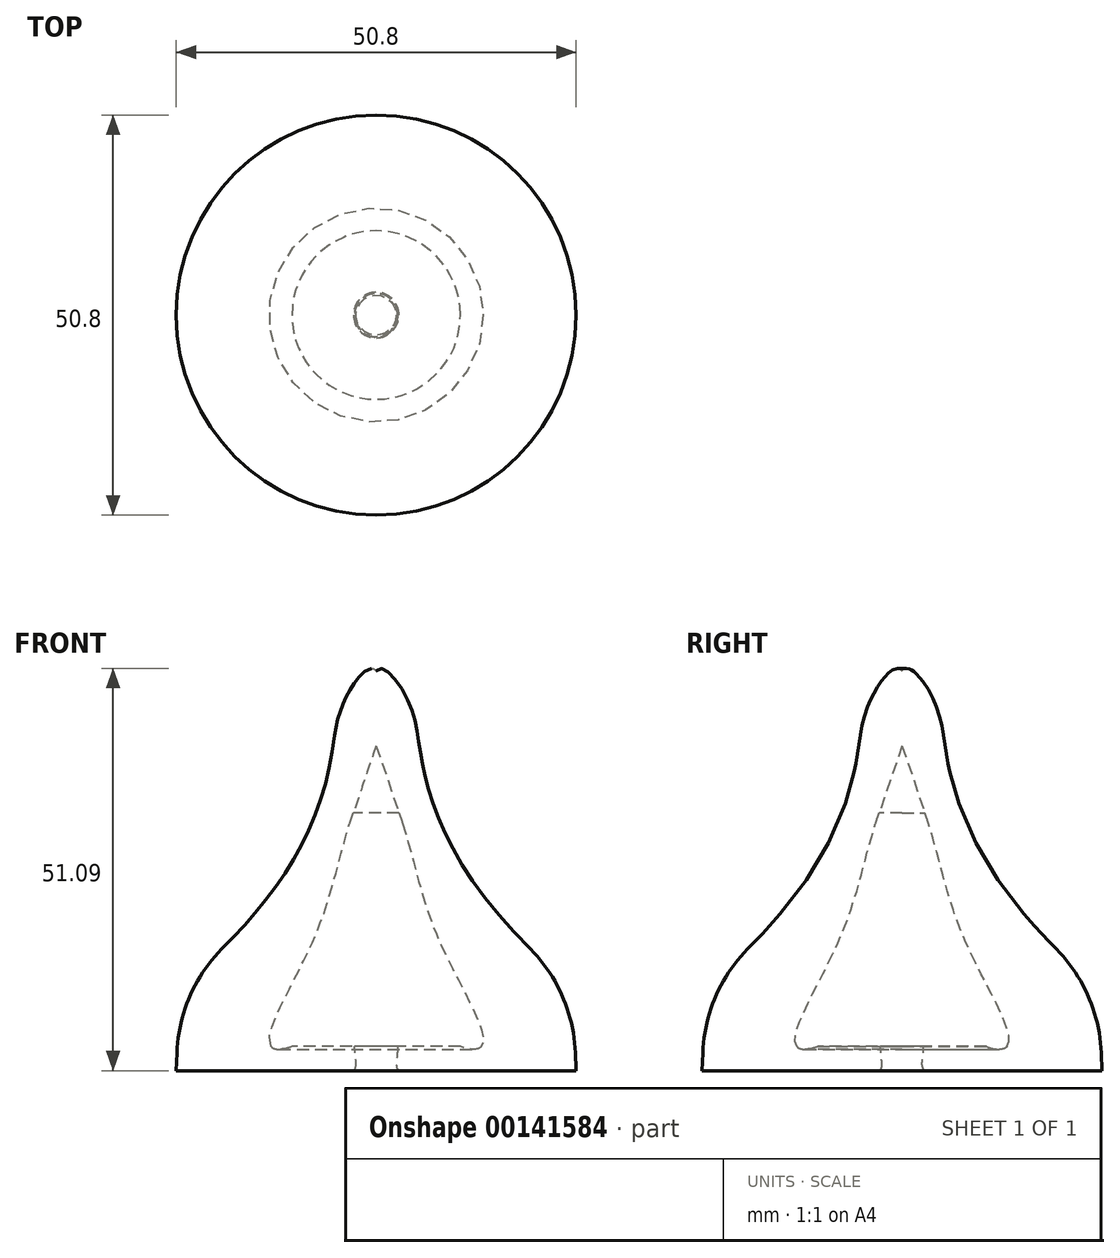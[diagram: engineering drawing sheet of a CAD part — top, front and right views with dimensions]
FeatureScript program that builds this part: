
annotation { "Feature Type Name" : "Feature", "Feature Type Description" : "" }
export const myFeature = defineFeature(function(context is Context, id is Id, definition is map)
    precondition{}
    {
        {
            var Q0;
            Q0=qCreatedBy(makeId("Front.planeOp"),FACE);
            var sketch = newSketch(context, id + "F0", { "sketchPlane" : qUnion([Q0])});
            skLineSegment(sketch, "E0", {"start": v(0, 50.8) * mm, "end": v(0, 41.27) * mm});
            skLineSegment(sketch, "E1", {"start": v(0, 0) * mm, "end": v(25.4, 0) * mm});
            skLineSegment(sketch, "E2", {"start": v(31.38, 0) * mm, "end": v(31.38, 0) * mm});
            skFitSpline(sketch, "E3", {"points": [v(0, 50.8) * mm, v(2.73, 3.36) * mm, v(2.7, 0.2) * mm, v(11.4, -5.62) * mm, v(31.2, -0.98) * mm, v(15.2, 20.23) * mm, v(5.9, 38.76) * mm, v(3.92, 47.28) * mm, v(0, 50.8) * mm]});
            skPoint(sketch, "E4.visualSharp", {"position": v(28.08, 6.56) * mm});
            skLineSegment(sketch, "E5", {"start": v(13.35, 3.06) * mm, "end": v(13.35, 3.06) * mm});
            skLineSegment(sketch, "E6", {"start": v(13.35, 3.06) * mm, "end": v(0, 3.06) * mm});
            skLineSegment(sketch, "E7", {"start": v(0, 3.06) * mm, "end": v(0, 0) * mm});
            skLineSegment(sketch, "E8", {"start": v(3.4, 31.28) * mm, "end": v(0, 41.27) * mm});
            skFitSpline(sketch, "E9", {"points": [v(0, 36.91) * mm, v(3.35, 31.43) * mm, v(8.19, 16.12) * mm, v(13.35, 3.06) * mm, v(1.22, 12.19) * mm, v(0, 36.91) * mm]});
            skLineSegment(sketch, "E10", {"start": v(25.31, 2.25) * mm, "end": v(25.4, 0) * mm});
            skLineSegment(sketch, "E11", {"start": v(0, 50.8) * mm, "end": v(0, 0) * mm, "construction": true});
            skPoint(sketch, "E12.visualSharp", {"position": v(25, 9.98) * mm});
            skArc(sketch, "E12.filletArc", {"start": v(25.31, 2.25) * mm, "mid": v(23.7, 9.38) * mm, "end": v(19.62, 15.45) * mm});
            skSolve(sketch);
        }
        {
            var Q0;
            Q0=makeQuery(id+"F0.imprint","IMPRINT",FACE,{"disambiguationData":[TD([[makeQuery(id+"F0.imprint","IMPRINT",EDGE,{"derivedFrom":sQuery(id+"F0.wireOp",EDGE,"E0")}),1.0]])]});
            var Q1;
            Q1=sQuery(id+"F0.wireOp",EDGE,"E7");
            revolve(context, id + "F1", {"entities" : qUnion([Q0]), "axis" : qUnion([Q1]), "revolveType" : RevolveType.FULL});
        }
    });
